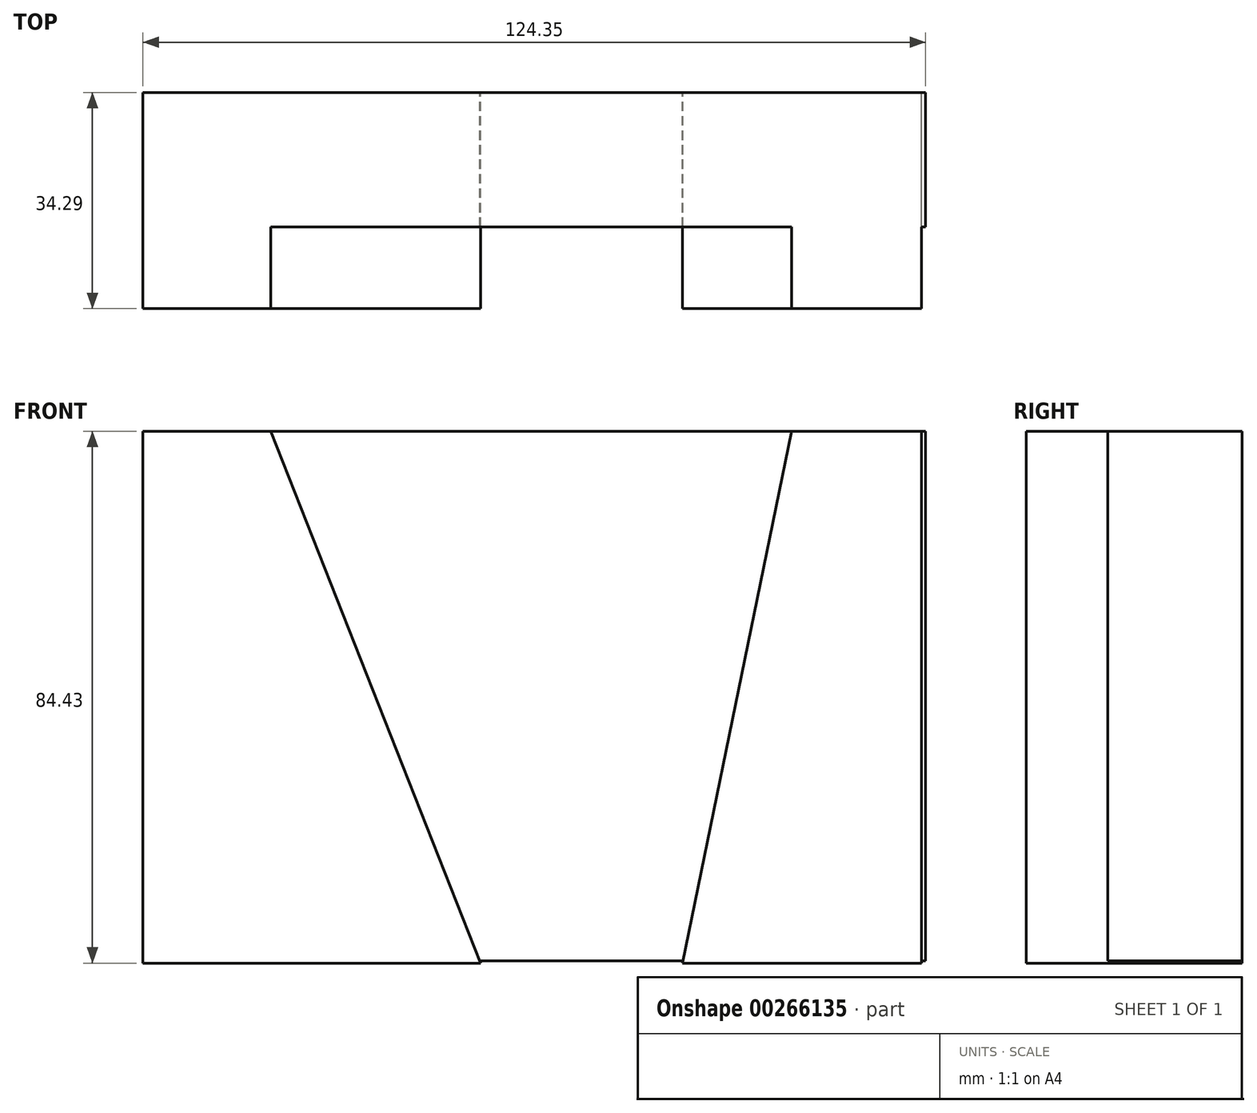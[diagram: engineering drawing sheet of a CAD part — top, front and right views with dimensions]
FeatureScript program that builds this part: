
annotation { "Feature Type Name" : "Feature", "Feature Type Description" : "" }
export const myFeature = defineFeature(function(context is Context, id is Id, definition is map)
    precondition{}
    {
        {
            var Q0;
            Q0=qCreatedBy(makeId("Front.planeOp"),FACE);
            var sketch = newSketch(context, id + "F0", { "sketchPlane" : qUnion([Q0])});
            skLineSegment(sketch, "E0.bottom", {"start": v(-63.48, 39.43) * mm, "end": v(60.87, 39.43) * mm});
            skLineSegment(sketch, "E0.top", {"start": v(-63.48, -44.67) * mm, "end": v(60.87, -44.67) * mm});
            skLineSegment(sketch, "E0.left", {"start": v(-63.48, 39.43) * mm, "end": v(-63.48, -44.67) * mm});
            skLineSegment(sketch, "E0.right", {"start": v(60.87, 39.43) * mm, "end": v(60.87, -44.67) * mm});
            skSolve(sketch);
        }
        {
            var Q0;
            Q0 = qSketchRegion(id + "F0", true);
            extrude(context, id + "F1", {"entities" : qUnion([Q0]), "depth" : 21.34 * mm});
        }
        {
            var Q0;
            Q0=qCreatedBy(makeId("Front.planeOp"),FACE);
            var sketch = newSketch(context, id + "F2", { "sketchPlane" : qUnion([Q0])});
            skLineSegment(sketch, "E1", {"start": v(-63.48, 39.43) * mm, "end": v(-63.48, -45) * mm});
            skLineSegment(sketch, "E2", {"start": v(-63.48, -45) * mm, "end": v(-9.82, -45) * mm});
            skLineSegment(sketch, "E3", {"start": v(-43.2, 39.43) * mm, "end": v(-63.48, 39.43) * mm});
            skLineSegment(sketch, "E4", {"start": v(-43.2, 39.43) * mm, "end": v(-9.82, -45) * mm});
            skLineSegment(sketch, "E5", {"start": v(60.21, 39.43) * mm, "end": v(60.21, -45) * mm});
            skLineSegment(sketch, "E6", {"start": v(60.21, -45) * mm, "end": v(22.25, -45) * mm});
            skLineSegment(sketch, "E7", {"start": v(60.21, 39.43) * mm, "end": v(39.6, 39.43) * mm});
            skLineSegment(sketch, "E8", {"start": v(39.6, 39.43) * mm, "end": v(22.25, -45) * mm});
            skSolve(sketch);
        }
        {
            var Q0;
            Q0 = qSketchRegion(id + "F2", true);
            extrude(context, id + "F3", {"entities" : qUnion([Q0]), "operationType" : NewBodyOperationType.ADD, "depth" : 34.3 * mm});
        }
    });
